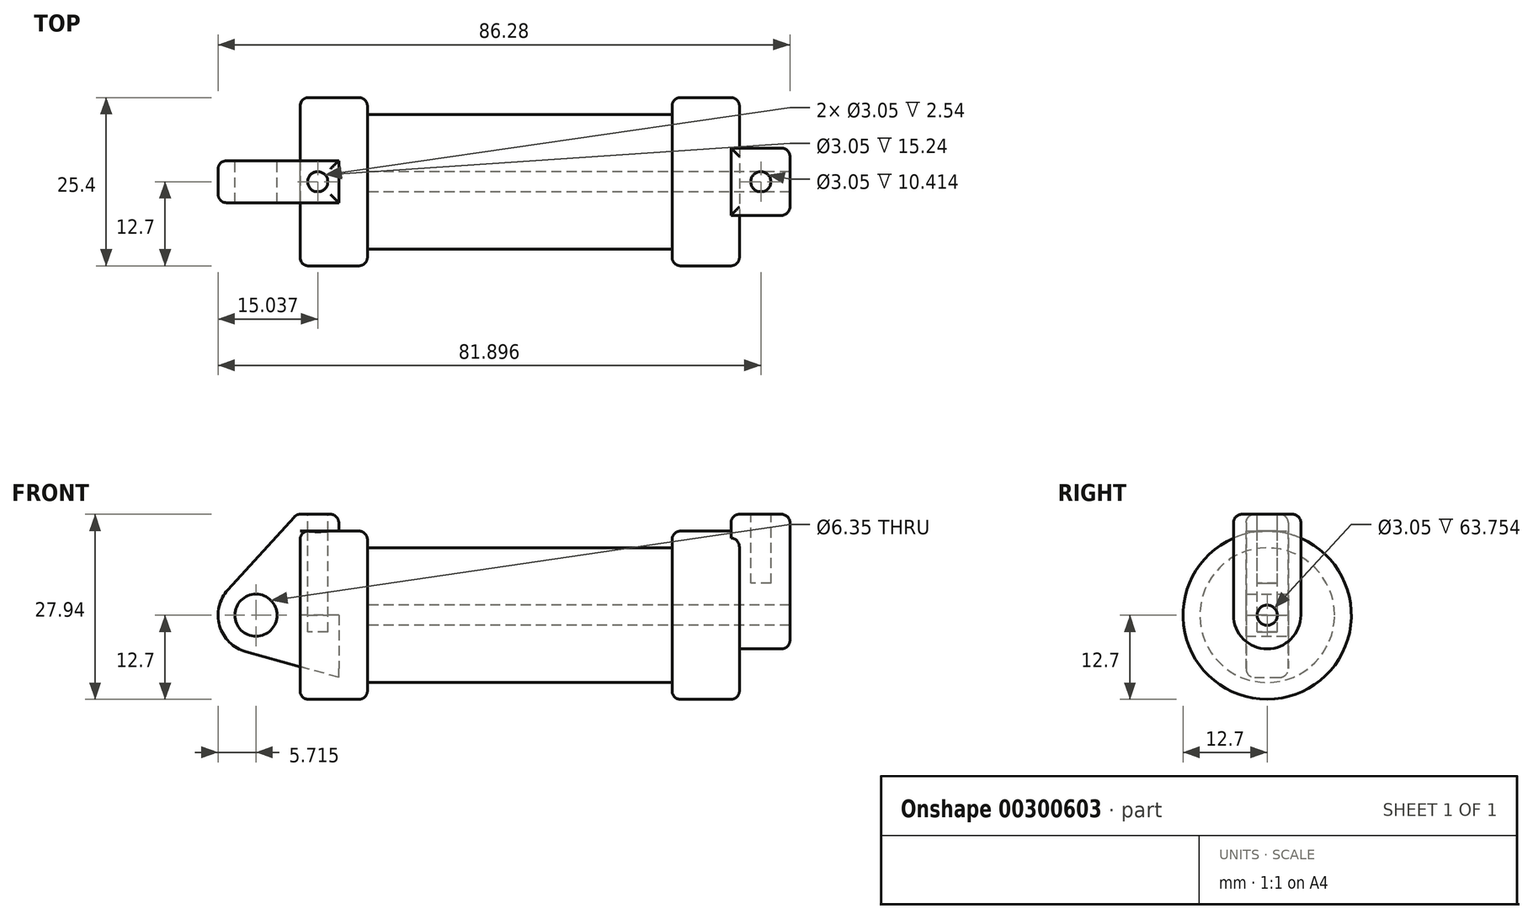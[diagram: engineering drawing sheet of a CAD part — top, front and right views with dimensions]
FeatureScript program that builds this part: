
annotation { "Feature Type Name" : "Feature", "Feature Type Description" : "" }
export const myFeature = defineFeature(function(context is Context, id is Id, definition is map)
    precondition{}
    {
        {
            var Q0;
            Q0=qCreatedBy(makeId("Front.planeOp"),FACE);
            var sketch = newSketch(context, id + "F0", { "sketchPlane" : qUnion([Q0])});
            skLineSegment(sketch, "E0", {"start": v(0, 0) * mm, "end": v(0, 12.7) * mm});
            skLineSegment(sketch, "E1", {"start": v(0, 12.7) * mm, "end": v(10.16, 12.7) * mm});
            skLineSegment(sketch, "E2", {"start": v(10.16, 12.7) * mm, "end": v(10.16, 10.16) * mm});
            skLineSegment(sketch, "E3", {"start": v(10.16, 10.16) * mm, "end": v(56.13, 10.16) * mm});
            skLineSegment(sketch, "E4", {"start": v(56.13, 10.16) * mm, "end": v(56.13, 12.7) * mm});
            skLineSegment(sketch, "E5", {"start": v(56.13, 12.7) * mm, "end": v(66.3, 12.7) * mm});
            skLineSegment(sketch, "E6", {"start": v(66.3, 12.7) * mm, "end": v(66.3, 0) * mm});
            skLineSegment(sketch, "E7", {"start": v(66.3, 0) * mm, "end": v(0, 0) * mm});
            skLineSegment(sketch, "E8", {"start": v(5.84, 15.24) * mm, "end": v(-0.5, 15.24) * mm});
            skLineSegment(sketch, "E9", {"start": v(-0.5, 15.24) * mm, "end": v(-10.88, 3.85) * mm});
            skLineSegment(sketch, "E10", {"start": v(0, 0) * mm, "end": v(-6.65, 0) * mm});
            skCircle(sketch, "E11", {"center": v(-6.65, 0) * mm, "radius": 5.72 * mm});
            skCircle(sketch, "E12", {"center": v(-6.65, 0) * mm, "radius": 3.18 * mm});
            skLineSegment(sketch, "E13", {"start": v(5.84, 15.24) * mm, "end": v(5.84, -9.4) * mm});
            skLineSegment(sketch, "E14", {"start": v(5.84, -9.4) * mm, "end": v(-8.18, -5.5) * mm});
            skSolve(sketch);
        }
        {
            var Q0;
            {var subQ0=sQuery(id+"F0.wireOp",EDGE,"E2");Q0=makeQuery(id+"F0.imprint","IMPRINT",FACE,{"disambiguationData":[TD([[makeQuery(id+"F0.imprint","IMPRINT",EDGE,{"derivedFrom":subQ0}),-1.0]])]});}
            var Q1;
            {var subQ0=sQuery(id+"F0.wireOp",EDGE,"E0");Q1=makeQuery(id+"F0.imprint","IMPRINT",FACE,{"disambiguationData":[TD([[makeQuery(id+"F0.imprint","IMPRINT",EDGE,{"derivedFrom":subQ0}),-1.0]])]});}
            var Q2;
            Q2=sQuery(id+"F0.wireOp",EDGE,"E7");
            revolve(context, id + "F1", {"entities" : qUnion([Q0, Q1]), "axis" : qUnion([Q2]), "revolveType" : RevolveType.FULL});
        }
        {
            var Q0;
            {var subQ1=sQuery(id+"F0.wireOp",EDGE,"E0");Q0=makeQuery(id+"F0.imprint","IMPRINT",FACE,{"disambiguationData":[TD([[makeQuery(id+"F0.imprint","IMPRINT",EDGE,{"derivedFrom":subQ1}),1.0]])]});}
            var Q1;
            {var subQ0=sQuery(id+"F0.wireOp",EDGE,"E14");Q1=makeQuery(id+"F0.imprint","IMPRINT",FACE,{"disambiguationData":[TD([[makeQuery(id+"F0.imprint","IMPRINT",EDGE,{"derivedFrom":subQ0}),-1.0]])]});}
            var Q2;
            {var subQ5=sQuery(id+"F0.wireOp",EDGE,"E12");Q2=makeQuery(id+"F0.imprint","IMPRINT",FACE,{"disambiguationData":[TD([[makeQuery(id+"F0.imprint","IMPRINT",EDGE,{"derivedFrom":subQ5}),-1.0]])]});}
            extrude(context, id + "F2", {"entities" : qUnion([Q0, Q1, Q2]), "endBound" : BoundingType.SYMMETRIC, "depth" : 6.35 * mm});
        }
        {
            var Q0;
            Q0=makeQuery(id+"F1.opRevolve","SWEPT_FACE",FACE,{"disambiguationData":[OSD([sQuery(id+"F0.wireOp",EDGE,"E6")])]});
            var sketch = newSketch(context, id + "F3", { "sketchPlane" : qUnion([Q0])});
            skCircle(sketch, "E15", {"center": v(0, 0) * mm, "radius": 1.52 * mm});
            skCircle(sketch, "E16", {"center": v(0, 0) * mm, "radius": 5.08 * mm});
            skLineSegment(sketch, "E17", {"start": v(0, 0) * mm, "end": v(12.7, 0) * mm, "construction": true});
            skLineSegment(sketch, "E18", {"start": v(0, 0) * mm, "end": v(-12.7, 0) * mm, "construction": true});
            skLineSegment(sketch, "E19", {"start": v(-5.08, 0) * mm, "end": v(-5.08, 15.24) * mm});
            skLineSegment(sketch, "E20", {"start": v(5.08, 0) * mm, "end": v(5.08, 15.24) * mm});
            skLineSegment(sketch, "E21", {"start": v(5.08, 15.24) * mm, "end": v(-5.08, 15.24) * mm});
            skSolve(sketch);
        }
        {
            var Q0;
            {var subQ0=sQuery(id+"F3.wireOp",EDGE,"E19");var subQ1=sQuery(id+"F3.wireOp",EDGE,"E16");var subQ2=makeQuery(id+"F3.imprint","INTERSECT",VERTEX,{"derivedFrom":[subQ1,subQ0]});Q0=makeQuery(id+"F3.imprint","IMPRINT",FACE,{"disambiguationData":[TD([[makeQuery(id+"F3.imprint","IMPRINT",EDGE,{"disambiguationData":[TD([[subQ2,1.0]])],"derivedFrom":subQ1}),-1.0]])]});}
            var Q1;
            {var subQ0=sQuery(id+"F3.wireOp",EDGE,"E21");Q1=makeQuery(id+"F3.imprint","IMPRINT",FACE,{"disambiguationData":[TD([[makeQuery(id+"F3.imprint","IMPRINT",EDGE,{"derivedFrom":subQ0}),1.0]])]});}
            var Q2;
            Q2=makeQuery(id+"F3.imprint","IMPRINT",FACE,{"disambiguationData":[TD([[makeQuery(id+"F3.imprint","IMPRINT",EDGE,{"derivedFrom":sQuery(id+"F3.wireOp",EDGE,"E15")}),-1.0]])]});
            extrude(context, id + "F4", {"entities" : qUnion([Q0, Q1, Q2]), "operationType" : NewBodyOperationType.ADD, "depth" : 7.62 * mm, "hasSecondDirection" : true, "secondDirectionOppositeDirection" : true, "secondDirectionDepth" : 1.27 * mm});
        }
        {
            var Q0;
            Q0=makeQuery(id+"F4.boolean.opBoolean","SPLIT",FACE,{"disambiguationData":[TD([makeQuery(id+"F4.opExtrude","SWEPT_FACE",FACE,{"disambiguationData":[OSD([sQuery(id+"F3.wireOp",EDGE,"E15")])]})])],"derivedFrom":makeQuery(id+"F1.opRevolve","SWEPT_FACE",FACE,{"disambiguationData":[OSD([sQuery(id+"F0.wireOp",EDGE,"E6")])]})});
            var Q1;
            Q1=makeQuery(id+"F1.opRevolve","SWEPT_FACE",FACE,{"disambiguationData":[OSD([sQuery(id+"F0.wireOp",EDGE,"E2")])]});
            extrude(context, id + "F5", {"entities" : qUnion([Q0]), "operationType" : NewBodyOperationType.REMOVE, "endBound" : BoundingType.UP_TO_SURFACE, "oppositeDirection" : true, "endBoundEntityFace" : qUnion([Q1]), "depth" : 25.4 * mm});
        }
        {
            var Q0;
            Q0=makeQuery(id+"F2.opExtrude","SWEPT_FACE",FACE,{"disambiguationData":[OSD([sQuery(id+"F0.wireOp",EDGE,"E8")])]});
            var sketch = newSketch(context, id + "F6", { "sketchPlane" : qUnion([Q0])});
            skLineSegment(sketch, "E22", {"start": v(2.67, 3.18) * mm, "end": v(2.67, -3.18) * mm, "construction": true});
            skLineSegment(sketch, "E23", {"start": v(5.84, 0) * mm, "end": v(-0.5, 0) * mm, "construction": true});
            skCircle(sketch, "E24", {"center": v(2.67, 0) * mm, "radius": 1.52 * mm});
            skLineSegment(sketch, "E25", {"start": v(73.8, 0) * mm, "end": v(56.17, 0) * mm, "construction": true});
            skCircle(sketch, "E26", {"center": v(69.53, 0) * mm, "radius": 1.52 * mm});
            skSolve(sketch);
        }
        {
            var Q0;
            Q0=makeQuery(id+"F6.imprint","IMPRINT",FACE,{"disambiguationData":[TD([[makeQuery(id+"F6.imprint","IMPRINT",EDGE,{"derivedFrom":sQuery(id+"F6.wireOp",EDGE,"E24")}),1.0]])]});
            extrude(context, id + "F7", {"entities" : qUnion([Q0]), "operationType" : NewBodyOperationType.REMOVE, "oppositeDirection" : true, "depth" : 17.78 * mm});
        }
        {
            var Q0;
            Q0=makeQuery(id+"F6.imprint","IMPRINT",FACE,{"disambiguationData":[TD([[makeQuery(id+"F6.imprint","IMPRINT",EDGE,{"derivedFrom":sQuery(id+"F6.wireOp",EDGE,"E26")}),1.0]])]});
            extrude(context, id + "F8", {"entities" : qUnion([Q0]), "operationType" : NewBodyOperationType.REMOVE, "oppositeDirection" : true, "depth" : 10.4 * mm});
        }
        {
            var Q0;
            Q0=makeQuery(id+"F1.opRevolve","SWEPT_EDGE",EDGE,{"disambiguationData":[OSD([sQuery(id+"F0.wireOp",EDGE,"E1"),sQuery(id+"F0.wireOp",EDGE,"E2")])]});
            var Q1;
            Q1=makeQuery(id+"F1.opRevolve","SWEPT_EDGE",EDGE,{"disambiguationData":[OSD([sQuery(id+"F0.wireOp",EDGE,"E0"),sQuery(id+"F0.wireOp",EDGE,"E1")])]});
            var Q2;
            Q2=makeQuery(id+"F1.opRevolve","SWEPT_EDGE",EDGE,{"disambiguationData":[OSD([sQuery(id+"F0.wireOp",EDGE,"E4"),sQuery(id+"F0.wireOp",EDGE,"E5")])]});
            var Q3;
            Q3=makeQuery(id+"F1.opRevolve","SWEPT_EDGE",EDGE,{"disambiguationData":[OSD([sQuery(id+"F0.wireOp",EDGE,"E5"),sQuery(id+"F0.wireOp",EDGE,"E6")])]});
            fillet(context, id + "F9", {"entities" : qUnion([Q0, Q1, Q2, Q3]), "radius" : 1.27 * mm, "tangentPropagation" : true, "allowEdgeOverflow" : false});
        }
        {
            var Q0;
            Q0=makeQuery(id+"F2.opExtrude","SWEPT_EDGE",EDGE,{"disambiguationData":[OSD([sQuery(id+"F0.wireOp",EDGE,"E8"),sQuery(id+"F0.wireOp",EDGE,"E13")])]});
            var Q1;
            Q1=makeQuery(id+"F2.opExtrude","CAP_EDGE",EDGE,{"disambiguationData":[OSD([sQuery(id+"F0.wireOp",EDGE,"E8")])],"isStart":true});
            var Q2;
            Q2=makeQuery(id+"F2.opExtrude","CAP_EDGE",EDGE,{"disambiguationData":[OSD([sQuery(id+"F0.wireOp",EDGE,"E8")])],"isStart":false});
            var Q3;
            Q3=makeQuery(id+"F2.opExtrude","CAP_EDGE",EDGE,{"disambiguationData":[OSD([sQuery(id+"F0.wireOp",EDGE,"E9")])],"isStart":false});
            var Q4;
            Q4=makeQuery(id+"F2.opExtrude","CAP_EDGE",EDGE,{"disambiguationData":[OSD([sQuery(id+"F0.wireOp",EDGE,"E9")])],"isStart":true});
            var Q5;
            Q5=makeQuery(id+"F2.opExtrude","SWEPT_EDGE",EDGE,{"disambiguationData":[OSD([sQuery(id+"F0.wireOp",EDGE,"E8"),sQuery(id+"F0.wireOp",EDGE,"E9")])]});
            fillet(context, id + "F10", {"entities" : qUnion([Q0, Q1, Q2, Q3, Q4, Q5]), "radius" : 1.27 * mm, "tangentPropagation" : true, "allowEdgeOverflow" : false});
        }
        {
            var Q0;
            Q0=makeQuery(id+"F4.opExtrude","CAP_EDGE",EDGE,{"disambiguationData":[OSD([sQuery(id+"F3.wireOp",EDGE,"E21")])],"isStart":true});
            var Q1;
            Q1=makeQuery(id+"F4.opExtrude","SWEPT_EDGE",EDGE,{"disambiguationData":[OSD([sQuery(id+"F3.wireOp",EDGE,"E19"),sQuery(id+"F3.wireOp",EDGE,"E21")])]});
            var Q2;
            Q2=makeQuery(id+"F4.opExtrude","CAP_EDGE",EDGE,{"disambiguationData":[OSD([sQuery(id+"F3.wireOp",EDGE,"E21")])],"isStart":false});
            var Q3;
            Q3=makeQuery(id+"F4.opExtrude","SWEPT_EDGE",EDGE,{"disambiguationData":[OSD([sQuery(id+"F3.wireOp",EDGE,"E20"),sQuery(id+"F3.wireOp",EDGE,"E21")])]});
            var Q4;
            Q4=makeQuery(id+"F4.opExtrude","CAP_EDGE",EDGE,{"disambiguationData":[OSD([sQuery(id+"F3.wireOp",EDGE,"E19")])],"isStart":false});
            var Q5;
            Q5=makeQuery(id+"F4.opExtrude","CAP_EDGE",EDGE,{"disambiguationData":[OSD([sQuery(id+"F3.wireOp",EDGE,"E20")])],"isStart":false});
            fillet(context, id + "F11", {"entities" : qUnion([Q0, Q1, Q2, Q3, Q4, Q5]), "radius" : 1.27 * mm, "tangentPropagation" : true, "allowEdgeOverflow" : false});
        }
    });
